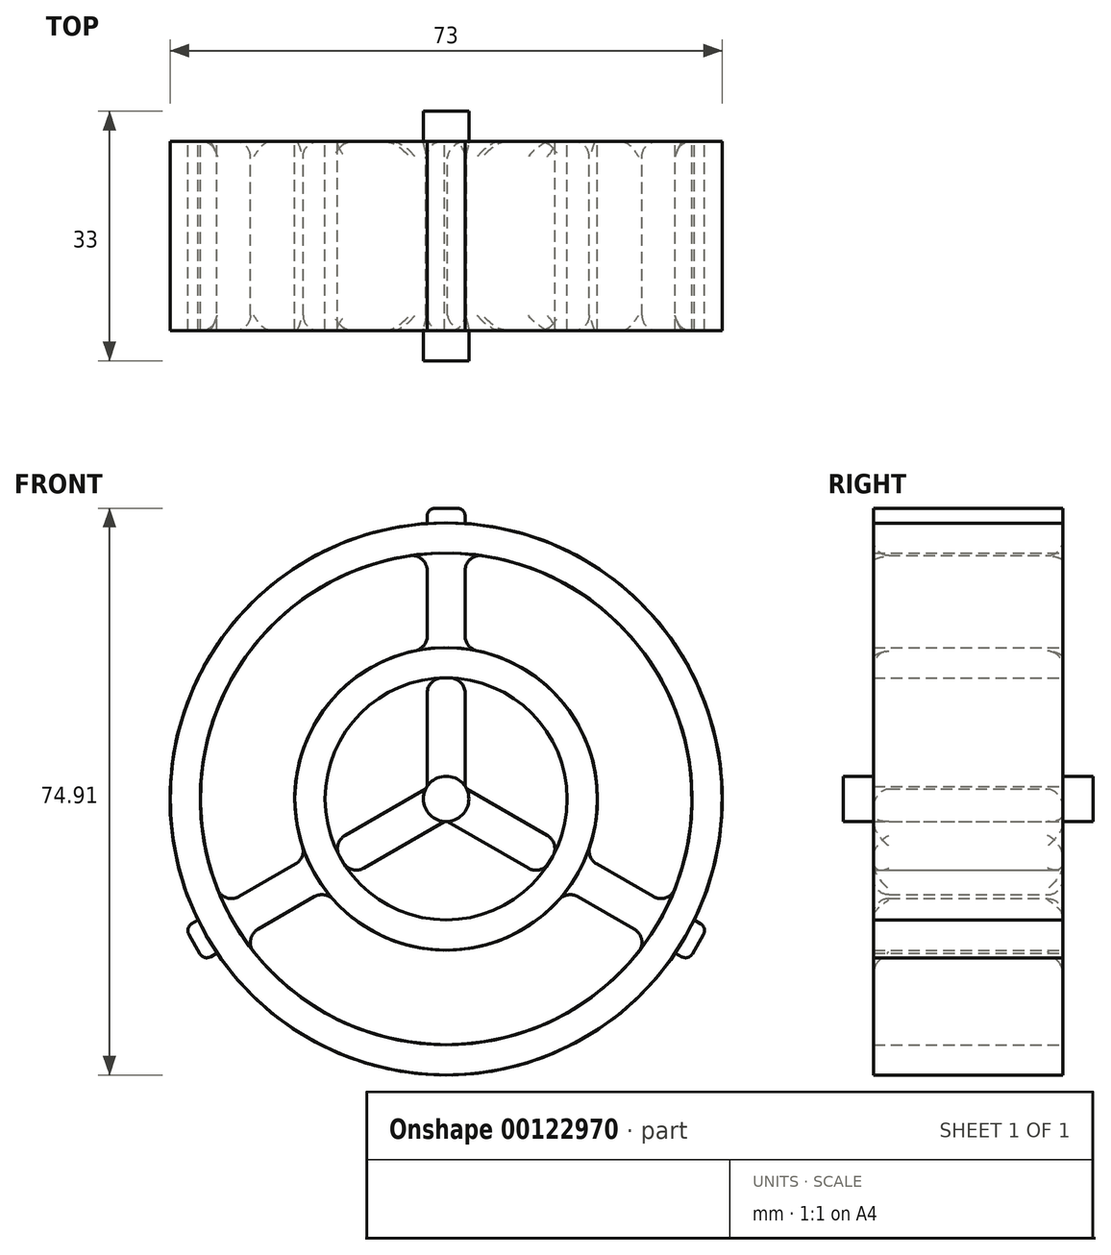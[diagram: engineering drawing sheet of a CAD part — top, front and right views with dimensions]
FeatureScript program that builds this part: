
annotation { "Feature Type Name" : "Feature", "Feature Type Description" : "" }
export const myFeature = defineFeature(function(context is Context, id is Id, definition is map)
    precondition{}
    {
        {
            var Q0;
            Q0=qCreatedBy(makeId("Front.planeOp"),FACE);
            var sketch = newSketch(context, id + "F0", { "sketchPlane" : qUnion([Q0])});
            skCircle(sketch, "E0", {"center": v(0, 0) * mm, "radius": 36.5 * mm});
            skCircle(sketch, "E1", {"center": v(0, 0) * mm, "radius": 32.5 * mm});
            skLineSegment(sketch, "E2.bottom", {"start": v(-2.5, 36.41) * mm, "end": v(2.5, 36.41) * mm});
            skLineSegment(sketch, "E2.top", {"start": v(-1.5, 38.41) * mm, "end": v(1.5, 38.41) * mm});
            skLineSegment(sketch, "E2.left", {"start": v(-2.5, 36.41) * mm, "end": v(-2.5, 37.41) * mm});
            skLineSegment(sketch, "E2.right", {"start": v(2.5, 36.41) * mm, "end": v(2.5, 37.41) * mm});
            skPoint(sketch, "E2.middle", {"position": v(0, 37.41) * mm});
            skPoint(sketch, "E3.visualSharp", {"position": v(-2.5, 38.41) * mm});
            skArc(sketch, "E3.filletArc", {"start": v(-1.5, 38.41) * mm, "mid": v(-2.2, 38.12) * mm, "end": v(-2.5, 37.41) * mm});
            skPoint(sketch, "E4.visualSharp", {"position": v(2.5, 38.41) * mm});
            skArc(sketch, "E4.filletArc", {"start": v(2.5, 37.41) * mm, "mid": v(2.2, 38.12) * mm, "end": v(1.5, 38.41) * mm});
            skCircle(sketch, "E5", {"center": v(0, 0) * mm, "radius": 20 * mm});
            skCircle(sketch, "E6", {"center": v(0, 0) * mm, "radius": 16 * mm});
            skLineSegment(sketch, "E7", {"start": v(-2.5, 32.4) * mm, "end": v(-2.5, 19.84) * mm});
            skLineSegment(sketch, "E8", {"start": v(2.5, 32.4) * mm, "end": v(2.5, 19.84) * mm});
            skCircle(sketch, "E9", {"center": v(0, 0) * mm, "radius": 3 * mm});
            skLineSegment(sketch, "E10", {"start": v(-2.5, 15.8) * mm, "end": v(-2.5, 1.66) * mm});
            skLineSegment(sketch, "E11", {"start": v(2.5, 15.8) * mm, "end": v(2.5, 1.66) * mm});
            skLineSegment(sketch, "E12.1.0", {"start": v(-14.94, -5.74) * mm, "end": v(-2.69, 1.34) * mm});
            skLineSegment(sketch, "E12.1.1", {"start": v(-12.44, -10.07) * mm, "end": v(-0.19, -3) * mm});
            skLineSegment(sketch, "E12.2.0", {"start": v(12.44, -10.07) * mm, "end": v(0.19, -3) * mm});
            skLineSegment(sketch, "E12.2.1", {"start": v(14.94, -5.74) * mm, "end": v(2.69, 1.34) * mm});
            skSolve(sketch);
        }
        {
            var Q0;
            Q0 = qSketchRegion(id + "F0", true);
            var Q1;
            Q1=makeQuery(id+"F0.imprint","IMPRINT",FACE,{"disambiguationData":[TD([[makeQuery(id+"F0.imprint","IMPRINT",EDGE,{"derivedFrom":sQuery(id+"F0.wireOp",EDGE,"E6")}),-1.0]])]});
            var Q2;
            {var subQ0=sQuery(id+"F0.wireOp",EDGE,"E7");Q2=makeQuery(id+"F0.imprint","IMPRINT",FACE,{"disambiguationData":[TD([[makeQuery(id+"F0.imprint","IMPRINT",EDGE,{"derivedFrom":subQ0}),1.0]])]});}
            extrude(context, id + "F1", {"entities" : qUnion([Q0, Q1, Q2]), "depth" : 25 * mm});
        }
        {
            var Q0;
            Q0=makeQuery(id+"F1.opExtrude","SWEPT_BODY",BODY,{"disambiguationData":[OSD([sQuery(id+"F0.wireOp",EDGE,"E0"),sQuery(id+"F0.wireOp",EDGE,"E1"),sQuery(id+"F0.wireOp",EDGE,"E2.top"),sQuery(id+"F0.wireOp",EDGE,"E2.left"),sQuery(id+"F0.wireOp",EDGE,"E2.right"),sQuery(id+"F0.wireOp",EDGE,"E3.filletArc"),sQuery(id+"F0.wireOp",EDGE,"E4.filletArc"),sQuery(id+"F0.wireOp",EDGE,"E5"),sQuery(id+"F0.wireOp",EDGE,"E6"),sQuery(id+"F0.wireOp",EDGE,"E7"),sQuery(id+"F0.wireOp",EDGE,"E8")])]});
            var Q1;
            Q1=makeQuery(id+"F1.opExtrude","CAP_EDGE",EDGE,{"disambiguationData":[OSD([sQuery(id+"F0.wireOp",EDGE,"E6")])],"isStart":false});
            circularPattern(context, id + "F2", {"entities" : qUnion([Q0]), "axis" : qUnion([Q1]), "angle" : 120 * degree, "instanceCount" : 3});
        }
        {
            var Q0;
            Q0=makeQuery(id+"F2.opPattern","COPY",EDGE,{"derivedFrom":makeQuery(id+"F1.opExtrude","SWEPT_EDGE",EDGE,{"disambiguationData":[OSD([sQuery(id+"F0.wireOp",EDGE,"E5"),sQuery(id+"F0.wireOp",EDGE,"E8")])]}),"instanceName":"2"});
            var Q1;
            Q1=makeQuery(id+"F2.opPattern","COPY",EDGE,{"derivedFrom":makeQuery(id+"F1.opExtrude","SWEPT_EDGE",EDGE,{"disambiguationData":[OSD([sQuery(id+"F0.wireOp",EDGE,"E5"),sQuery(id+"F0.wireOp",EDGE,"E7")])]}),"instanceName":"1"});
            var Q2;
            Q2=makeQuery(id+"F2.opPattern","COPY",EDGE,{"derivedFrom":makeQuery(id+"F1.opExtrude","SWEPT_EDGE",EDGE,{"disambiguationData":[OSD([sQuery(id+"F0.wireOp",EDGE,"E1"),sQuery(id+"F0.wireOp",EDGE,"E7")])]}),"instanceName":"1"});
            var Q3;
            Q3=makeQuery(id+"F2.opPattern","COPY",EDGE,{"derivedFrom":makeQuery(id+"F1.opExtrude","CAP_EDGE",EDGE,{"disambiguationData":[OSD([sQuery(id+"F0.wireOp",EDGE,"E7")])],"isStart":false}),"instanceName":"1"});
            var Q4;
            Q4=makeQuery(id+"F2.opPattern","COPY",EDGE,{"derivedFrom":makeQuery(id+"F1.opExtrude","CAP_EDGE",EDGE,{"disambiguationData":[OSD([sQuery(id+"F0.wireOp",EDGE,"E8")])],"isStart":false}),"instanceName":"2"});
            var Q5;
            Q5=makeQuery(id+"F2.opPattern","COPY",EDGE,{"derivedFrom":makeQuery(id+"F1.opExtrude","SWEPT_EDGE",EDGE,{"disambiguationData":[OSD([sQuery(id+"F0.wireOp",EDGE,"E1"),sQuery(id+"F0.wireOp",EDGE,"E8")])]}),"instanceName":"2"});
            var Q6;
            Q6=makeQuery(id+"F2.opPattern","COPY",EDGE,{"derivedFrom":makeQuery(id+"F1.opExtrude","SWEPT_EDGE",EDGE,{"disambiguationData":[OSD([sQuery(id+"F0.wireOp",EDGE,"E5"),sQuery(id+"F0.wireOp",EDGE,"E8")])]}),"instanceName":"1"});
            var Q7;
            Q7=makeQuery(id+"F2.opPattern","COPY",EDGE,{"derivedFrom":makeQuery(id+"F1.opExtrude","CAP_EDGE",EDGE,{"disambiguationData":[OSD([sQuery(id+"F0.wireOp",EDGE,"E8")])],"isStart":false}),"instanceName":"1"});
            var Q8;
            Q8=makeQuery(id+"F2.opPattern","COPY",EDGE,{"derivedFrom":makeQuery(id+"F1.opExtrude","SWEPT_EDGE",EDGE,{"disambiguationData":[OSD([sQuery(id+"F0.wireOp",EDGE,"E1"),sQuery(id+"F0.wireOp",EDGE,"E8")])]}),"instanceName":"1"});
            var Q9;
            Q9=makeQuery(id+"F1.opExtrude","SWEPT_EDGE",EDGE,{"disambiguationData":[OSD([sQuery(id+"F0.wireOp",EDGE,"E1"),sQuery(id+"F0.wireOp",EDGE,"E7")])]});
            var Q10;
            Q10=makeQuery(id+"F1.opExtrude","CAP_EDGE",EDGE,{"disambiguationData":[OSD([sQuery(id+"F0.wireOp",EDGE,"E7")])],"isStart":false});
            var Q11;
            Q11=makeQuery(id+"F1.opExtrude","SWEPT_EDGE",EDGE,{"disambiguationData":[OSD([sQuery(id+"F0.wireOp",EDGE,"E5"),sQuery(id+"F0.wireOp",EDGE,"E7")])]});
            var Q12;
            Q12=makeQuery(id+"F2.opPattern","COPY",EDGE,{"derivedFrom":makeQuery(id+"F1.opExtrude","CAP_EDGE",EDGE,{"disambiguationData":[OSD([sQuery(id+"F0.wireOp",EDGE,"E7")])],"isStart":false}),"instanceName":"2"});
            var Q13;
            Q13=makeQuery(id+"F2.opPattern","COPY",EDGE,{"derivedFrom":makeQuery(id+"F1.opExtrude","SWEPT_EDGE",EDGE,{"disambiguationData":[OSD([sQuery(id+"F0.wireOp",EDGE,"E5"),sQuery(id+"F0.wireOp",EDGE,"E7")])]}),"instanceName":"2"});
            var Q14;
            Q14=makeQuery(id+"F2.opPattern","COPY",EDGE,{"derivedFrom":makeQuery(id+"F1.opExtrude","SWEPT_EDGE",EDGE,{"disambiguationData":[OSD([sQuery(id+"F0.wireOp",EDGE,"E1"),sQuery(id+"F0.wireOp",EDGE,"E7")])]}),"instanceName":"2"});
            var Q15;
            Q15=makeQuery(id+"F1.opExtrude","SWEPT_EDGE",EDGE,{"disambiguationData":[OSD([sQuery(id+"F0.wireOp",EDGE,"E5"),sQuery(id+"F0.wireOp",EDGE,"E8")])]});
            var Q16;
            Q16=makeQuery(id+"F1.opExtrude","CAP_EDGE",EDGE,{"disambiguationData":[OSD([sQuery(id+"F0.wireOp",EDGE,"E8")])],"isStart":false});
            var Q17;
            Q17=makeQuery(id+"F1.opExtrude","CAP_EDGE",EDGE,{"disambiguationData":[OSD([sQuery(id+"F0.wireOp",EDGE,"E8")])],"isStart":true});
            var Q18;
            Q18=makeQuery(id+"F1.opExtrude","CAP_EDGE",EDGE,{"disambiguationData":[OSD([sQuery(id+"F0.wireOp",EDGE,"E8")])],"isStart":false});
            var Q19;
            Q19=makeQuery(id+"F2.opPattern","COPY",EDGE,{"derivedFrom":makeQuery(id+"F1.opExtrude","CAP_EDGE",EDGE,{"disambiguationData":[OSD([sQuery(id+"F0.wireOp",EDGE,"E7")])],"isStart":true}),"instanceName":"2"});
            var Q20;
            Q20=makeQuery(id+"F2.opPattern","COPY",EDGE,{"derivedFrom":makeQuery(id+"F1.opExtrude","CAP_EDGE",EDGE,{"disambiguationData":[OSD([sQuery(id+"F0.wireOp",EDGE,"E8")])],"isStart":true}),"instanceName":"2"});
            var Q21;
            Q21=makeQuery(id+"F2.opPattern","COPY",EDGE,{"derivedFrom":makeQuery(id+"F1.opExtrude","CAP_EDGE",EDGE,{"disambiguationData":[OSD([sQuery(id+"F0.wireOp",EDGE,"E8")])],"isStart":true}),"instanceName":"1"});
            var Q22;
            Q22=makeQuery(id+"F2.opPattern","COPY",EDGE,{"derivedFrom":makeQuery(id+"F1.opExtrude","CAP_EDGE",EDGE,{"disambiguationData":[OSD([sQuery(id+"F0.wireOp",EDGE,"E7")])],"isStart":true}),"instanceName":"1"});
            var Q23;
            Q23=makeQuery(id+"F1.opExtrude","CAP_EDGE",EDGE,{"disambiguationData":[OSD([sQuery(id+"F0.wireOp",EDGE,"E7")])],"isStart":true});
            var Q24;
            Q24=makeQuery(id+"F1.opExtrude","SWEPT_EDGE",EDGE,{"disambiguationData":[OSD([sQuery(id+"F0.wireOp",EDGE,"E1"),sQuery(id+"F0.wireOp",EDGE,"E8")])]});
            fillet(context, id + "F3", {"entities" : qUnion([Q0, Q1, Q2, Q3, Q4, Q5, Q6, Q7, Q8, Q9, Q10, Q11, Q12, Q13, Q14, Q15, Q16, Q17, Q18, Q19, Q20, Q21, Q22, Q23, Q24]), "radius" : 2 * mm, "tangentPropagation" : true, "allowEdgeOverflow" : false});
        }
        {
            var Q0;
            {var subQ0=sQuery(id+"F0.wireOp",EDGE,"E12.1.0");Q0=makeQuery(id+"F0.imprint","IMPRINT",FACE,{"disambiguationData":[TD([[makeQuery(id+"F0.imprint","IMPRINT",EDGE,{"derivedFrom":subQ0}),-1.0]])]});}
            var Q1;
            {var subQ0=sQuery(id+"F0.wireOp",EDGE,"E10");Q1=makeQuery(id+"F0.imprint","IMPRINT",FACE,{"disambiguationData":[TD([[makeQuery(id+"F0.imprint","IMPRINT",EDGE,{"derivedFrom":subQ0}),1.0]])]});}
            var Q2;
            {var subQ0=sQuery(id+"F0.wireOp",EDGE,"E12.2.0");Q2=makeQuery(id+"F0.imprint","IMPRINT",FACE,{"disambiguationData":[TD([[makeQuery(id+"F0.imprint","IMPRINT",EDGE,{"derivedFrom":subQ0}),-1.0]])]});}
            extrude(context, id + "F4", {"entities" : qUnion([Q0, Q1, Q2]), "depth" : 25 * mm});
        }
        {
            var Q0;
            {var subQ0=sQuery(id+"F0.wireOp",EDGE,"E9");var subQ5=makeQuery(id+"F0.imprint","INTERSECT",VERTEX,{"derivedFrom":[sQuery(id+"F0.wireOp",EDGE,"E12.1.1"),subQ0]});Q0=makeQuery(id+"F0.imprint","IMPRINT",FACE,{"disambiguationData":[TD([[makeQuery(id+"F0.imprint","IMPRINT",EDGE,{"disambiguationData":[TD([[subQ5,-1.0]])],"derivedFrom":subQ0}),1.0]])]});}
            extrude(context, id + "F5", {"entities" : qUnion([Q0]), "depth" : 29 * mm});
        }
        {
            var Q0;
            {var subQ0=sQuery(id+"F0.wireOp",EDGE,"E9");var subQ5=makeQuery(id+"F0.imprint","INTERSECT",VERTEX,{"derivedFrom":[sQuery(id+"F0.wireOp",EDGE,"E12.1.1"),subQ0]});Q0=makeQuery(id+"F0.imprint","IMPRINT",FACE,{"disambiguationData":[TD([[makeQuery(id+"F0.imprint","IMPRINT",EDGE,{"disambiguationData":[TD([[subQ5,-1.0]])],"derivedFrom":subQ0}),1.0]])]});}
            extrude(context, id + "F6", {"entities" : qUnion([Q0]), "operationType" : NewBodyOperationType.ADD, "oppositeDirection" : true, "depth" : 4 * mm});
        }
        {
            var Q0;
            Q0=makeQuery(id+"F4.opExtrude","SWEPT_EDGE",EDGE,{"disambiguationData":[OSD([sQuery(id+"F0.wireOp",EDGE,"E6"),sQuery(id+"F0.wireOp",EDGE,"E12.1.0")])]});
            var Q1;
            Q1=makeQuery(id+"F4.opExtrude","SWEPT_EDGE",EDGE,{"disambiguationData":[OSD([sQuery(id+"F0.wireOp",EDGE,"E6"),sQuery(id+"F0.wireOp",EDGE,"E12.1.1")])]});
            var Q2;
            Q2=makeQuery(id+"F4.opExtrude","SWEPT_EDGE",EDGE,{"disambiguationData":[OSD([sQuery(id+"F0.wireOp",EDGE,"E6"),sQuery(id+"F0.wireOp",EDGE,"E12.2.1")])]});
            var Q3;
            Q3=makeQuery(id+"F4.opExtrude","SWEPT_EDGE",EDGE,{"disambiguationData":[OSD([sQuery(id+"F0.wireOp",EDGE,"E6"),sQuery(id+"F0.wireOp",EDGE,"E12.2.0")])]});
            var Q4;
            Q4=makeQuery(id+"F4.opExtrude","SWEPT_EDGE",EDGE,{"disambiguationData":[OSD([sQuery(id+"F0.wireOp",EDGE,"E6"),sQuery(id+"F0.wireOp",EDGE,"E10")])]});
            var Q5;
            Q5=makeQuery(id+"F4.opExtrude","SWEPT_EDGE",EDGE,{"disambiguationData":[OSD([sQuery(id+"F0.wireOp",EDGE,"E6"),sQuery(id+"F0.wireOp",EDGE,"E11")])]});
            var Q6;
            Q6=makeQuery(id+"F4.opExtrude","CAP_EDGE",EDGE,{"disambiguationData":[OSD([sQuery(id+"F0.wireOp",EDGE,"E12.2.0")])],"isStart":true});
            var Q7;
            Q7=makeQuery(id+"F4.opExtrude","CAP_EDGE",EDGE,{"disambiguationData":[OSD([sQuery(id+"F0.wireOp",EDGE,"E12.2.1")])],"isStart":true});
            var Q8;
            Q8=makeQuery(id+"F4.opExtrude","CAP_EDGE",EDGE,{"disambiguationData":[OSD([sQuery(id+"F0.wireOp",EDGE,"E12.1.0")])],"isStart":true});
            var Q9;
            Q9=makeQuery(id+"F4.opExtrude","CAP_EDGE",EDGE,{"disambiguationData":[OSD([sQuery(id+"F0.wireOp",EDGE,"E12.2.1")])],"isStart":false});
            var Q10;
            Q10=makeQuery(id+"F4.opExtrude","CAP_EDGE",EDGE,{"disambiguationData":[OSD([sQuery(id+"F0.wireOp",EDGE,"E12.2.0")])],"isStart":false});
            var Q11;
            Q11=makeQuery(id+"F4.opExtrude","CAP_EDGE",EDGE,{"disambiguationData":[OSD([sQuery(id+"F0.wireOp",EDGE,"E12.1.0")])],"isStart":false});
            fillet(context, id + "F7", {"entities" : qUnion([Q0, Q1, Q2, Q3, Q4, Q5, Q6, Q7, Q8, Q9, Q10, Q11]), "radius" : 2 * mm, "tangentPropagation" : true, "allowEdgeOverflow" : false});
        }
    });
